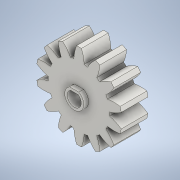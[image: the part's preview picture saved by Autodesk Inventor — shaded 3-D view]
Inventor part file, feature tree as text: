
AUTODESK INVENTOR PART (.ipt)
format: ipt  version: 2020 (Build 240168000, 168)  size: 229,376 bytes
history: native  units: mm (DEFAULTED — no unit token found)
features: sketch x4, extrude x3, plane x3, other x3
ambient origin geometry x8: Origin, YZ Plane, XZ Plane, XY Plane, X Axis, Y Axis, Z Axis, Center Point
bodies: Solid1 (feature_tree)
feature tree (13):
  extrude  "Extrusion1"  Depth=12.7mm TaperAngle=0.0deg
  plane  "Work Plane1"
  plane  "Work Plane2"
  plane  "Work Plane3"
  other  "Spur Gear"
  extrude  "Extrusion2"  Depth=76.2mm TaperAngle=0.0deg
  extrude  "Extrusion3"  TaperAngle=0.0deg  [1 undecoded]
  sketch  "Sketch1"  dims[d0=40.64mm d1=12.7mm d2=0.0mm]
  sketch  "Sketch2"  dims[d3=35.56mm d4=76.2mm d5=0.0mm]
  other  "Srf1"
  sketch  "Sketch3"  dims[d6=0.0mm d7=2.243995mm d9=0.0mm]
  sketch  "Sketch4"  dims[d14=0.0mm d15=124.46mm d16=0.0mm d17=0.0mm d18=0.0mm d19=124.46mm d20=6.35mm d21=5.8mm d22=0.15mm d23=25.4mm d24=0.0mm d25=1.2mm d26=2.286mm d27=0.0mm]
  other  "Pitch Diameter"
note: 1 required parameter value undecoded (feature->parameter linkage not recoverable at this tier; creation-order binding heuristic only, values carry confidence <= 0.55)
